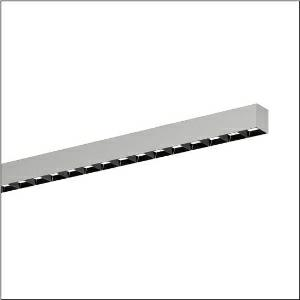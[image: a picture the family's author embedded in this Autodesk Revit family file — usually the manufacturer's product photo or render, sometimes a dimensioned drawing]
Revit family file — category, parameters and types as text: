
# Revit family: silica_r__21_51mx24tat4s_af2d
name_source: partatom
category: Lighting Fixtures
units: mm (PartAtom-declared; Revit-internal decimal feet)

## family parameters
Cut with Voids When Loaded = No
Host = Face
Light Source = No
Part Type = Normal
Room Calculation Point = No
Round Connector Dimension = Use Diameter
Shared = No

## types (1)
- --- (1 x LED, 3280 lm, 32.4 W, 6500K)
    Apparent Load = 32 VA
    CIE Flux Codes = 74 94 99 100 100
    Color Rendering = 80
    Color Temperature = 6500K
    Default Elevation = 1800 mm
    Description = Silica® 21, office luminaire, primary light control with darklight reflector, of PMMA, black, light emission: direct distribution, primary light characteristic: asymmetric, installation type: surface-mounted, LED, rated luminous flux: 3.280lm, luminous efficacy: 96lm/W, light colour: 8tw, colour temperature: 2700..6500K, control gear: DALI DT8, with terminal, 3+2-pole, max. 2.5mm², mains connection: 220..240V, AC, 50/60Hz, rated input power: 34.1W, luminaire housing, of aluminium, metallic grey (RAL 9006), length: 1.204mm, width: 53mm, height: 53mm, protection rating (complete): IP20, insulation class (complete): insulation class I (protective earthing), certification: CE, permissible operating ambient temperature: 0..+35°C, standard: EN 50419, packaging unit: 1 piece
    Height = 53 mm
    Lamp = 1 x LED
    Lamp Light Flux = 3280 lm
    Lamp Power = 32.4 W
    Lamp count = 1
    Length = 1204 mm
    Luminous efficacy = 101 lm/W
    Manufacturer = Siteco
    ModVariant = No
    Model = 51MX24TAT4S
    Mounting Place = Ceiling
    Mounting Type = Surface mounted
    Number of Poles = 1
    OnlyDefault = Yes
    Power Factor = 1
    Product Name = Silica® 21
    Product group = office luminaire | ceiling mounted
    ProductGroupID = 302
    Protection Class = Protection class I
    Protection Degree = IP 20
    RLX_Detail_Level = 1
    RLX_Emergency_Light_Flux = 0 lm
    RLX_Emergency_Type = 0
    RLX_Emergency_Type_DB = No
    RlxData = <blob elided: 39761 chars, md5=bdf33628>
    Socket = socket
    Standby Power = 0 W
    System Light Flux = 3280 lm
    System Power = 32 W
    Type Comments = individual setting
    Type Image = l_1335929.jpg
    URL = http://relux.com
    VarID = @adj_139980
    Voltage = 0 V
    Weight = 0.00 kg
    Width = 53 mm

## geometry (parser evidence)
native form markers: Blend x4, Sweep x9
no freeform markers — native parametric forms only
